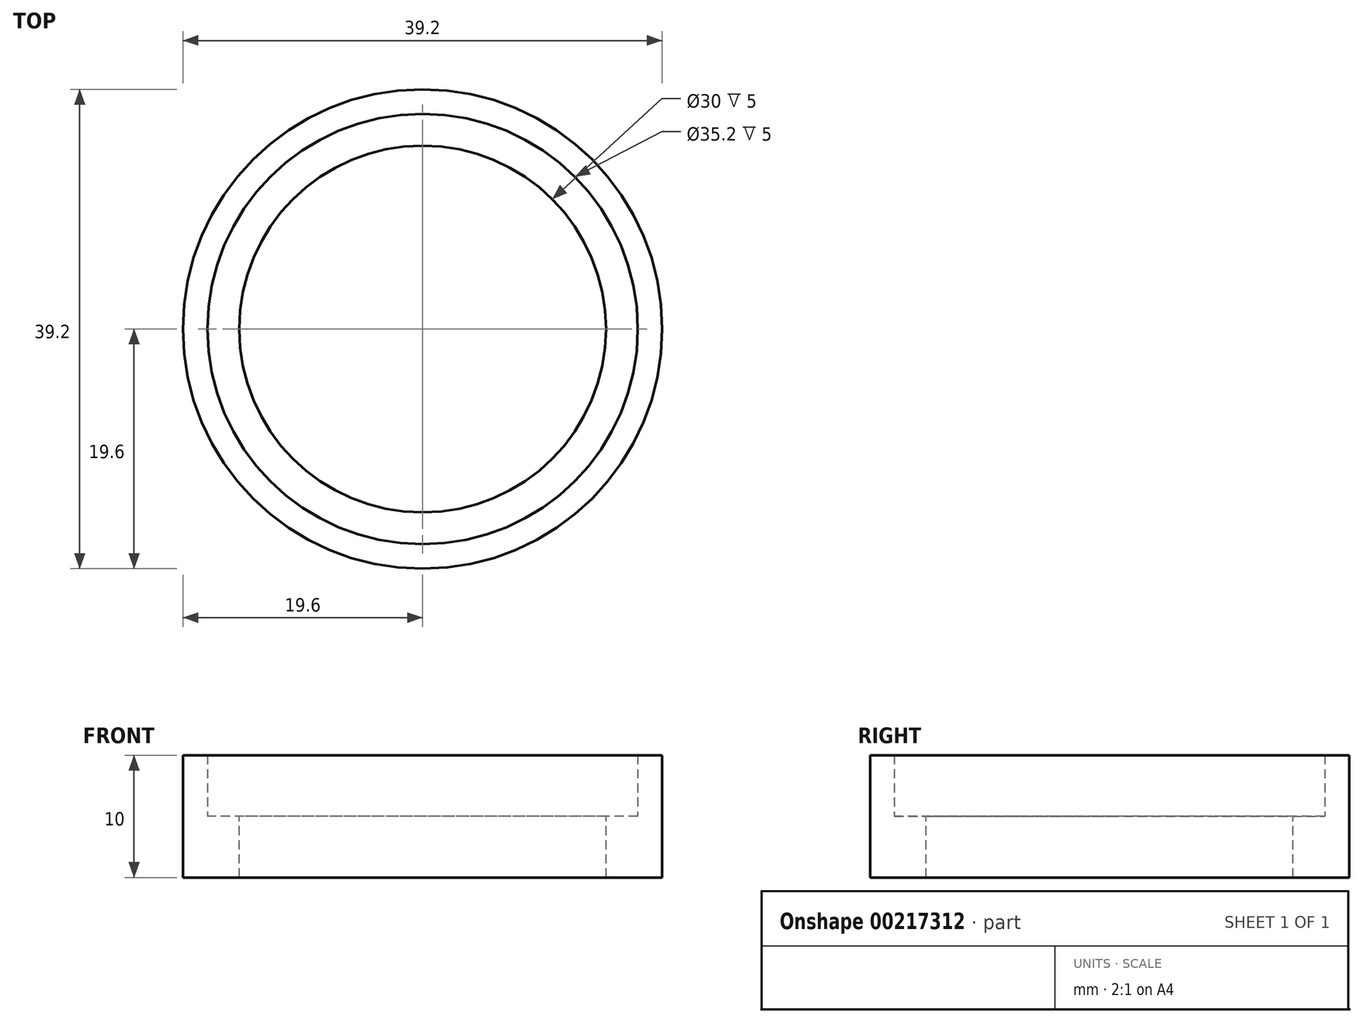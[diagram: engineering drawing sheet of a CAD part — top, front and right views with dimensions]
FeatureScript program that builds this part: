
annotation { "Feature Type Name" : "Feature", "Feature Type Description" : "" }
export const myFeature = defineFeature(function(context is Context, id is Id, definition is map)
    precondition{}
    {
        {
            var Q0;
            Q0=qCreatedBy(makeId("Top.planeOp"),FACE);
            var sketch = newSketch(context, id + "F0", { "sketchPlane" : qUnion([Q0])});
            skCircle(sketch, "E0", {"center": v(0, 0) * mm, "radius": 15 * mm});
            skCircle(sketch, "E1", {"center": v(0, 0) * mm, "radius": 17 * mm});
            skCircle(sketch, "E2", {"center": v(0, 0) * mm, "radius": 17.6 * mm});
            skCircle(sketch, "E3", {"center": v(0, 0) * mm, "radius": 19.6 * mm});
            skSolve(sketch);
        }
        {
            var Q0;
            Q0=makeQuery(id+"F0.imprint","IMPRINT",FACE,{"disambiguationData":[TD([[makeQuery(id+"F0.imprint","IMPRINT",EDGE,{"derivedFrom":sQuery(id+"F0.wireOp",EDGE,"E2")}),-1.0]])]});
            var Q1;
            Q1=makeQuery(id+"F0.imprint","IMPRINT",FACE,{"disambiguationData":[TD([[makeQuery(id+"F0.imprint","IMPRINT",EDGE,{"derivedFrom":sQuery(id+"F0.wireOp",EDGE,"E1")}),-1.0]])]});
            var Q2;
            Q2=makeQuery(id+"F0.imprint","IMPRINT",FACE,{"disambiguationData":[TD([[makeQuery(id+"F0.imprint","IMPRINT",EDGE,{"derivedFrom":sQuery(id+"F0.wireOp",EDGE,"E0")}),-1.0]])]});
            extrude(context, id + "F1", {"entities" : qUnion([Q0, Q1, Q2]), "oppositeDirection" : true, "depth" : 5 * mm});
        }
        {
            var Q0;
            Q0=makeQuery(id+"F0.imprint","IMPRINT",FACE,{"disambiguationData":[TD([[makeQuery(id+"F0.imprint","IMPRINT",EDGE,{"derivedFrom":sQuery(id+"F0.wireOp",EDGE,"E2")}),-1.0]])]});
            extrude(context, id + "F2", {"entities" : qUnion([Q0]), "operationType" : NewBodyOperationType.ADD, "depth" : 5 * mm});
        }
    });
